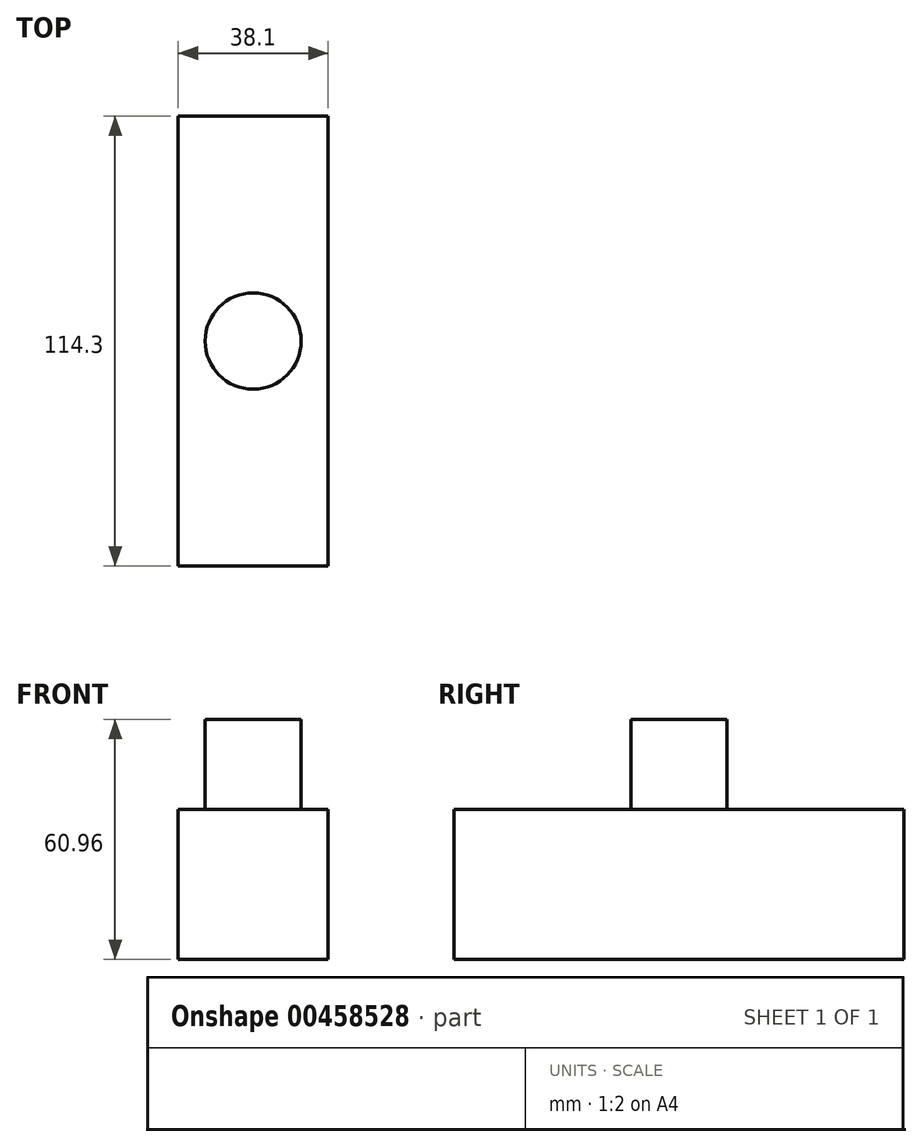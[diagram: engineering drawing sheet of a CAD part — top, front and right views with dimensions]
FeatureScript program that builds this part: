
annotation { "Feature Type Name" : "Feature", "Feature Type Description" : "" }
export const myFeature = defineFeature(function(context is Context, id is Id, definition is map)
    precondition{}
    {
        {
            var Q0;
            Q0=qCreatedBy(makeId("Right.planeOp"),FACE);
            var sketch = newSketch(context, id + "F0", { "sketchPlane" : qUnion([Q0])});
            skLineSegment(sketch, "E0.bottom", {"start": v(-57.15, -19.05) * mm, "end": v(57.15, -19.05) * mm});
            skLineSegment(sketch, "E0.top", {"start": v(-57.15, 19.05) * mm, "end": v(57.15, 19.05) * mm});
            skLineSegment(sketch, "E0.left", {"start": v(-57.15, -19.05) * mm, "end": v(-57.15, 19.05) * mm});
            skLineSegment(sketch, "E0.right", {"start": v(57.15, -19.05) * mm, "end": v(57.15, 19.05) * mm});
            skPoint(sketch, "E0.middle", {"position": v(0, 0) * mm});
            skSolve(sketch);
        }
        {
            var Q0;
            Q0=qCreatedBy(makeId("Top.planeOp"),FACE);
            var sketch = newSketch(context, id + "F1", { "sketchPlane" : qUnion([Q0])});
            skCircle(sketch, "E1", {"center": v(0, 0) * mm, "radius": 12.2 * mm});
            skSolve(sketch);
        }
        {
            var Q0;
            Q0 = qSketchRegion(id + "F1", true);
            extrude(context, id + "F2", {"entities" : qUnion([Q0]), "depth" : 41.9 * mm});
        }
        {
            var Q0;
            Q0=makeQuery(id+"F0.imprint","IMPRINT",FACE,{"disambiguationData":[TD([[makeQuery(id+"F0.imprint","IMPRINT",EDGE,{"derivedFrom":sQuery(id+"F0.wireOp",EDGE,"E0.bottom")}),1.0]])]});
            extrude(context, id + "F3", {"entities" : qUnion([Q0]), "operationType" : NewBodyOperationType.ADD, "endBound" : BoundingType.SYMMETRIC, "depth" : 38.1 * mm});
        }
    });
